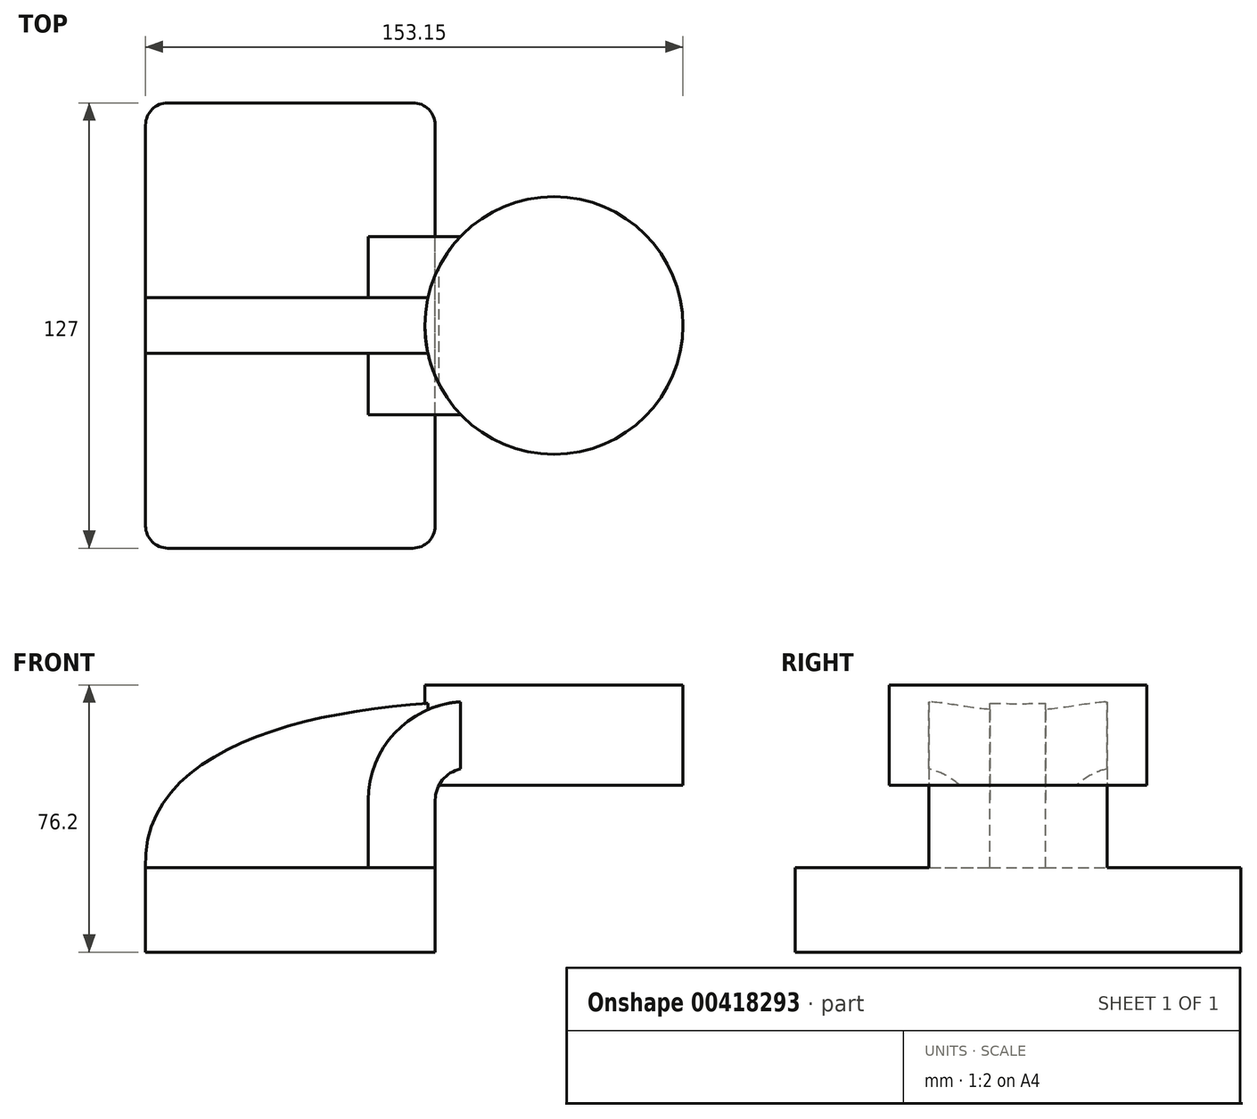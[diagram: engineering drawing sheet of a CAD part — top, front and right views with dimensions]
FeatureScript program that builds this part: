
annotation { "Feature Type Name" : "Feature", "Feature Type Description" : "" }
export const myFeature = defineFeature(function(context is Context, id is Id, definition is map)
    precondition{}
    {
        {
            var Q0;
            Q0=qCreatedBy(makeId("Front.planeOp"),FACE);
            var sketch = newSketch(context, id + "F0", { "sketchPlane" : qUnion([Q0])});
            skLineSegment(sketch, "E0.bottom", {"start": v(41.28, -12.04) * mm, "end": v(-41.28, -12.04) * mm});
            skLineSegment(sketch, "E0.top", {"start": v(41.28, 12.04) * mm, "end": v(-41.28, 12.04) * mm});
            skLineSegment(sketch, "E0.left", {"start": v(41.28, -12.04) * mm, "end": v(41.28, 12.04) * mm});
            skLineSegment(sketch, "E0.right", {"start": v(-41.28, -12.04) * mm, "end": v(-41.28, 12.04) * mm});
            skPoint(sketch, "E0.middle", {"position": v(0, 0) * mm});
            skLineSegment(sketch, "E1.bottom", {"start": v(61.05, 35.59) * mm, "end": v(111.85, 35.59) * mm});
            skLineSegment(sketch, "E1.top", {"start": v(61.05, 64.16) * mm, "end": v(111.85, 64.16) * mm});
            skLineSegment(sketch, "E1.left", {"start": v(61.05, 35.59) * mm, "end": v(61.05, 64.16) * mm});
            skLineSegment(sketch, "E1.right", {"start": v(111.85, 35.59) * mm, "end": v(111.85, 64.16) * mm});
            skPoint(sketch, "E1.middle", {"position": v(86.45, 49.87) * mm});
            skLineSegment(sketch, "E2", {"start": v(41.28, 12.04) * mm, "end": v(41.28, 31.3) * mm});
            skArc(sketch, "E3", {"start": v(41.28, 31.3) * mm, "mid": v(43.93, 37.7) * mm, "end": v(50.35, 40.36) * mm});
            skLineSegment(sketch, "E4", {"start": v(50.35, 40.36) * mm, "end": v(75.1, 40.36) * mm});
            skLineSegment(sketch, "E5.0", {"start": v(50.35, 59.41) * mm, "end": v(75.1, 59.41) * mm});
            skArc(sketch, "E5.1", {"start": v(22.23, 31.3) * mm, "mid": v(30.46, 51.18) * mm, "end": v(50.35, 59.41) * mm});
            skLineSegment(sketch, "E5.2", {"start": v(22.23, 12.04) * mm, "end": v(22.23, 31.3) * mm});
            skLineSegment(sketch, "E6", {"start": v(75.1, 64.16) * mm, "end": v(75.1, 35.59) * mm});
            skFitSpline(sketch, "E7", {"points": [v(-41.28, 12.04) * mm, v(61.05, 59.41) * mm], "startDerivative": vector(-4.57, 116.36) * mm, "endDerivative": vector(125.65, -2.32) * mm});
            skSolve(sketch);
        }
        {
            var Q0;
            Q0=makeQuery(id+"F0.imprint","IMPRINT",FACE,{"disambiguationData":[TD([[makeQuery(id+"F0.imprint","IMPRINT",EDGE,{"derivedFrom":sQuery(id+"F0.wireOp",EDGE,"E0.bottom")}),-1.0]])]});
            extrude(context, id + "F1", {"entities" : qUnion([Q0]), "endBound" : BoundingType.SYMMETRIC, "depth" : 127 * mm});
        }
        {
            var Q0;
            {var subQ1=sQuery(id+"F0.wireOp",EDGE,"E2");Q0=makeQuery(id+"F0.imprint","IMPRINT",FACE,{"disambiguationData":[TD([[makeQuery(id+"F0.imprint","IMPRINT",EDGE,{"derivedFrom":subQ1}),1.0]])]});}
            var Q1;
            {var subQ3=sQuery(id+"F0.wireOp",EDGE,"E4");var subQ5=sQuery(id+"F0.wireOp",EDGE,"E6");var subQ6=makeQuery(id+"F0.imprint","INTERSECT",VERTEX,{"derivedFrom":[subQ3,subQ5]});Q1=makeQuery(id+"F0.imprint","IMPRINT",FACE,{"disambiguationData":[TD([[makeQuery(id+"F0.imprint","IMPRINT",EDGE,{"disambiguationData":[TD([[subQ6,1.0]])],"derivedFrom":subQ3}),1.0]])]});}
            extrude(context, id + "F2", {"entities" : qUnion([Q0, Q1]), "operationType" : NewBodyOperationType.ADD, "endBound" : BoundingType.SYMMETRIC, "depth" : 50.8 * mm});
        }
        {
            var Q0;
            {var subQ3=sQuery(id+"F0.wireOp",EDGE,"E5.2");Q0=makeQuery(id+"F0.imprint","IMPRINT",FACE,{"disambiguationData":[TD([[makeQuery(id+"F0.imprint","IMPRINT",EDGE,{"derivedFrom":subQ3}),1.0]])]});}
            extrude(context, id + "F3", {"entities" : qUnion([Q0]), "operationType" : NewBodyOperationType.ADD, "endBound" : BoundingType.SYMMETRIC, "depth" : 15.88 * mm});
        }
        {
            var Q0;
            {var subQ0=sQuery(id+"F0.wireOp",EDGE,"E1.right");Q0=makeQuery(id+"F0.imprint","IMPRINT",FACE,{"disambiguationData":[TD([[makeQuery(id+"F0.imprint","IMPRINT",EDGE,{"derivedFrom":subQ0}),1.0]])]});}
            var Q1;
            Q1=sQuery(id+"F0.wireOp",EDGE,"E6");
            revolve(context, id + "F4", {"operationType" : NewBodyOperationType.ADD, "entities" : qUnion([Q0]), "axis" : qUnion([Q1]), "revolveType" : RevolveType.FULL});
        }
        {
            var Q0;
            Q0=makeQuery(id+"F1.opExtrude","CAP_EDGE",EDGE,{"disambiguationData":[OSD([sQuery(id+"F0.wireOp",EDGE,"E0.left")])],"isStart":false});
            var Q1;
            Q1=makeQuery(id+"F1.opExtrude","CAP_EDGE",EDGE,{"disambiguationData":[OSD([sQuery(id+"F0.wireOp",EDGE,"E0.right")])],"isStart":false});
            var Q2;
            Q2=makeQuery(id+"F1.opExtrude","CAP_EDGE",EDGE,{"disambiguationData":[OSD([sQuery(id+"F0.wireOp",EDGE,"E0.left")])],"isStart":true});
            var Q3;
            Q3=makeQuery(id+"F1.opExtrude","CAP_EDGE",EDGE,{"disambiguationData":[OSD([sQuery(id+"F0.wireOp",EDGE,"E0.right")])],"isStart":true});
            fillet(context, id + "F5", {"entities" : qUnion([Q0, Q1, Q2, Q3]), "radius" : 6.35 * mm, "tangentPropagation" : true, "allowEdgeOverflow" : false});
        }
    });
